# Revit family: Kabelrinne_LKSU_ungelocht_Russia
name_source: partatom
category: Generic Models
revit_build: Autodesk Revit 2015 (Build: 20140606_1530(x64)
units: mm (PartAtom-declared; Revit-internal decimal feet)

## types (7) — shared parameters
H = 60 mm  [stored 0.19685 ft]
Manufacturer = OBO Bettermann
Material = Steel, Galvanized
URL = http://www.obo-bettermann.com
X = 14 mm  [stored 0.0459318 ft]

## per-type parameters (varying)
| type | "B" Dimension | GTIN | Manufacturer Art. No. |
| LKSU 610 FS RU | 100 mm  [stored 0.328084 ft] | 4012196561629 | 6048940 |
| LKSU 615 FS RU | 150 mm | 4012196649389 | 6048942 |
| LKSU 620 FS RU | 200 mm  [stored 0.656168 ft] | 4012196561636 | 6048944 |
| LKSU 630 FS RU | 300 mm | 4012196561643 | 6048948 |
| LKSU 640 FS RU | 400 mm  [stored 1.31234 ft] | 4012196625918 | 6048950 |
| LKSU 650 FS RU | 500 mm  [stored 1.64042 ft] | 4012196625925 | 6048954 |
| LKSU 660 FS RU | 600 mm | 4012196625932 | 6048956 |

note: column(s) folded — value = type name in every type: Article Type

note: [stored X ft] marks values corroborated as IEEE doubles in the binary element streams (Revit-internal decimal feet)

## geometry (parser evidence)
native form markers: Sweep x2
no freeform markers — native parametric forms only
